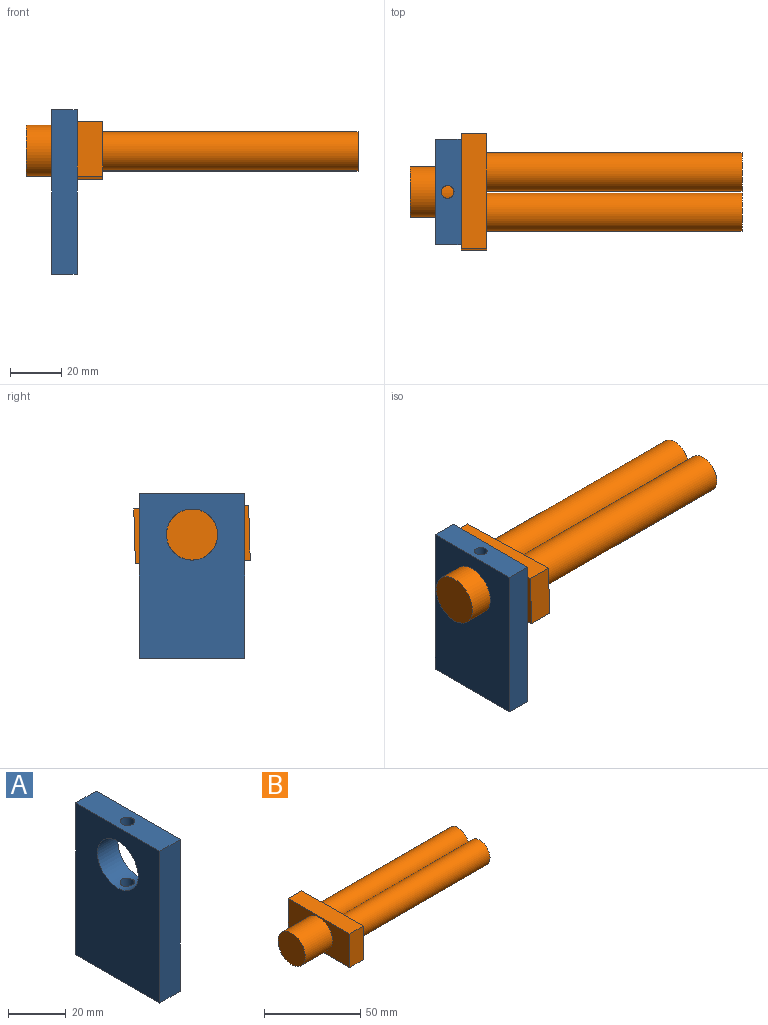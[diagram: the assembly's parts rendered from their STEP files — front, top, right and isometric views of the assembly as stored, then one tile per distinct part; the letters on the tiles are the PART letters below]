
ASSEMBLY  parts=2 mates=1
PART A: 10 faces, bbox 10x41.2x64.4 mm
  f0: plane 64.45x10mm, normal (0,1,0), area 644.5mm2, adj f1,f3,f5,f6
  f1: plane 41.21x10mm, normal (0,0,1), area 392.4mm2, adj f0,f2,f5,f6,f9
  f2: plane 64.45x10mm, normal (0,-1,0), area 644.5mm2, adj f1,f3,f5,f6
  f3: plane 41.21x10mm, normal (0,0,-1), area 412.1mm2, adj f0,f2,f5,f6
  f4: cylinder r=10mm len=20mm, axis (-1,0,0), area 588.8mm2, adj f5,f6,f8,f9
  f5: plane 64.45x41.21mm, normal (1,0,0), area 2341.4mm2, adj f0,f1,f2,f3,f4
  f6: plane 64.45x41.21mm, normal (-1,0,0), area 2341.4mm2, adj f0,f1,f2,f3,f4
  f7: plane 5x5mm, normal (0,0,1), area 19.6mm2, adj f8
  f8: cylinder r=2.5mm len=5mm, axis (0,0,1), area 65.5mm2, adj f4,f7
  f9: cylinder r=2.5mm len=6.31mm, axis (0,0,1), area 96.5mm2, adj f1,f4
PART B: 12 faces, bbox 130x45x21.3 mm
  f0: plane 44.99x10mm, normal (0,0,1), area 449.9mm2, adj f1,f3,f4,f5
  f1: plane 21.33x10mm, normal (0,-1,0), area 213.3mm2, adj f0,f2,f4,f5
  f2: plane 44.99x10mm, normal (0,0,-1), area 449.9mm2, adj f1,f3,f4,f5
  f3: plane 21.33x10mm, normal (0,1,0), area 213.3mm2, adj f0,f2,f4,f5
  f4: plane 44.99x21.33mm, normal (1,0,0), area 606.1mm2, adj f0,f1,f2,f3,f6,f8
  f5: plane 44.99x21.33mm, normal (-1,0,0), area 645.3mm2, adj f0,f1,f2,f3,f10
  f6: cylinder r=7.5mm len=100mm, axis (-1,0,0), area 4712.4mm2, adj f4,f7
  f7: plane 15x15mm, normal (1,0,0), area 176.7mm2, adj f6
  f8: cylinder r=7.5mm len=100mm, axis (-1,0,0), area 4712.4mm2, adj f4,f9
  f9: plane 15x15mm, normal (1,0,0), area 176.7mm2, adj f8
  f10: cylinder r=10mm len=20mm, axis (1,0,0), area 1256.6mm2, adj f5,f11
  f11: plane 20x20mm, normal (-1,0,0), area 314.2mm2, adj f10
PLACE A t=(-42.42,391.88,224.9)mm fixed
PLACE B rot(axis=(1,0,0),178.3deg) t=(-32.42,282.98,200.68)mm
MATE revolute B.f10 <-> A.f4  axis (-1,0,0) through (-32.42,296.89,209.49)mm
